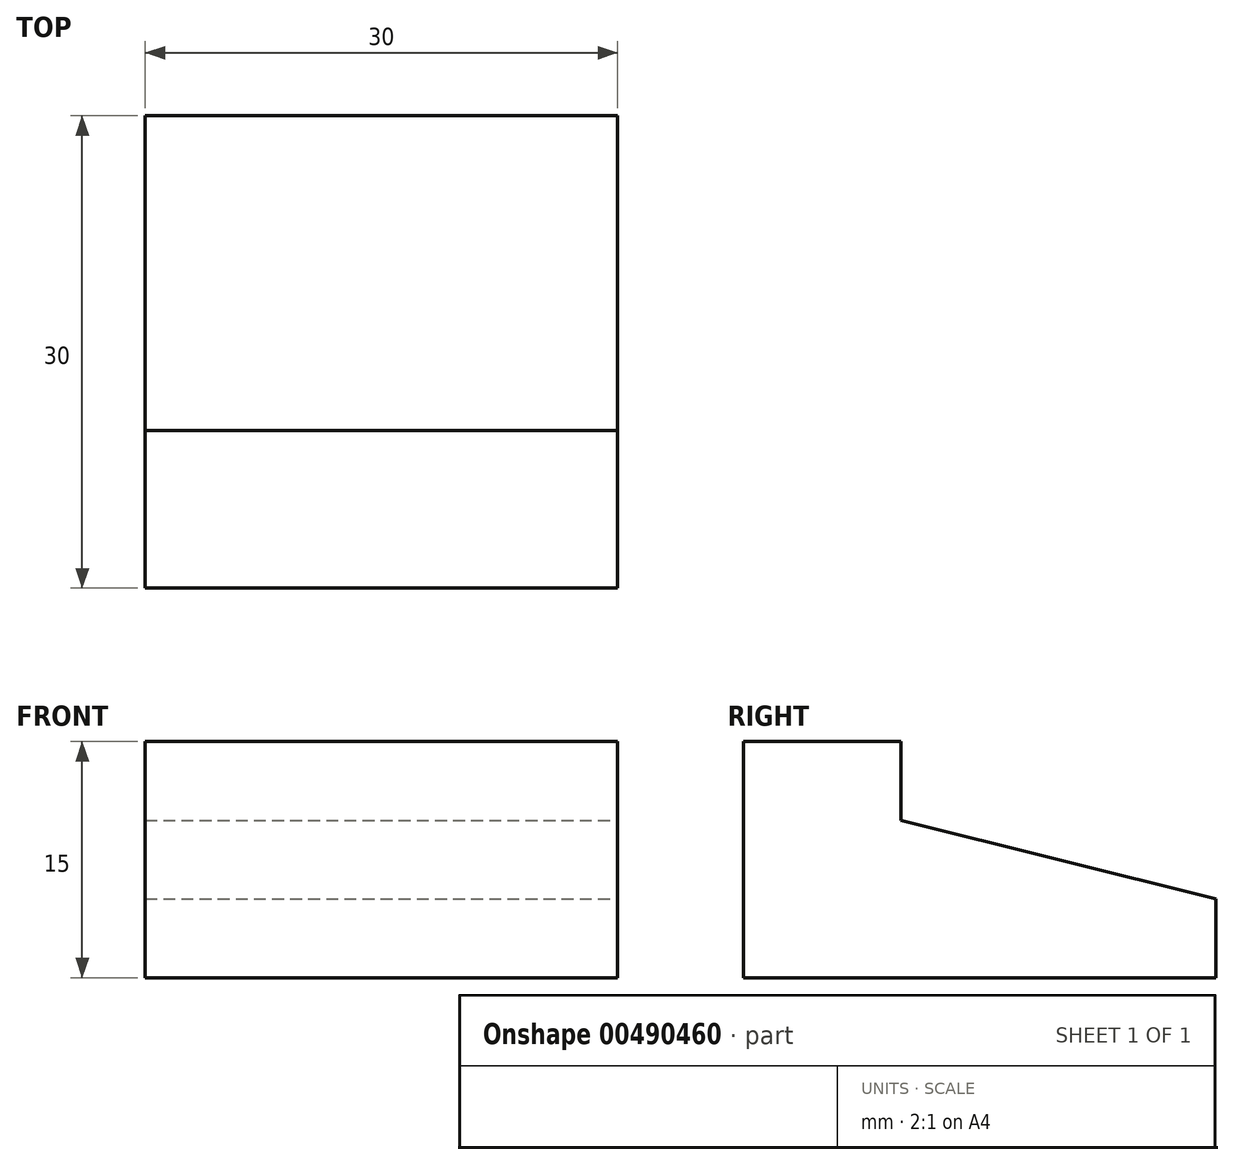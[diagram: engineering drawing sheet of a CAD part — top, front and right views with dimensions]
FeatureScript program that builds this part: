
annotation { "Feature Type Name" : "Feature", "Feature Type Description" : "" }
export const myFeature = defineFeature(function(context is Context, id is Id, definition is map)
    precondition{}
    {
        {
            var Q0;
            Q0=qCreatedBy(makeId("Top.planeOp"),FACE);
            var sketch = newSketch(context, id + "F0", { "sketchPlane" : qUnion([Q0])});
            skLineSegment(sketch, "E0.bottom", {"start": v(-46.78, 47.62) * mm, "end": v(-16.78, 47.62) * mm});
            skLineSegment(sketch, "E0.top", {"start": v(-46.78, 17.62) * mm, "end": v(-16.78, 17.62) * mm});
            skLineSegment(sketch, "E0.left", {"start": v(-46.78, 47.62) * mm, "end": v(-46.78, 17.62) * mm});
            skLineSegment(sketch, "E0.right", {"start": v(-16.78, 47.62) * mm, "end": v(-16.78, 17.62) * mm});
            skSolve(sketch);
        }
        {
            var Q0;
            Q0 = qSketchRegion(id + "F0", true);
            extrude(context, id + "F1", {"entities" : qUnion([Q0]), "depth" : 15 * mm});
        }
        {
            var Q0;
            Q0=makeQuery(id+"F1.opExtrude","SWEPT_FACE",FACE,{"disambiguationData":[OSD([sQuery(id+"F0.wireOp",EDGE,"E0.right")])]});
            var sketch = newSketch(context, id + "F2", { "sketchPlane" : qUnion([Q0])});
            skLineSegment(sketch, "E1", {"start": v(47.62, 0) * mm, "end": v(47.62, 5) * mm});
            skLineSegment(sketch, "E2", {"start": v(47.62, 5) * mm, "end": v(27.62, 10) * mm});
            skLineSegment(sketch, "E3", {"start": v(27.62, 10) * mm, "end": v(27.62, 15) * mm});
            skLineSegment(sketch, "E4", {"start": v(27.62, 15) * mm, "end": v(17.62, 15) * mm});
            skSolve(sketch);
        }
        {
            var Q0;
            {var subQ0=sQuery(id+"F2.wireOp",EDGE,"E2");Q0=makeQuery(id+"F2.imprint","IMPRINT",FACE,{"disambiguationData":[TD([[makeQuery(id+"F2.imprint","IMPRINT",EDGE,{"derivedFrom":subQ0}),-1.0]])]});}
            extrude(context, id + "F3", {"entities" : qUnion([Q0]), "operationType" : NewBodyOperationType.REMOVE, "endBound" : BoundingType.THROUGH_ALL, "oppositeDirection" : true, "depth" : 25 * mm});
        }
    });
